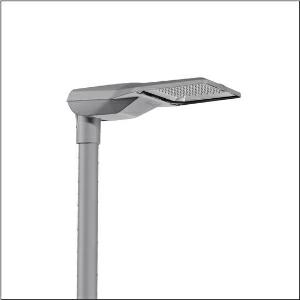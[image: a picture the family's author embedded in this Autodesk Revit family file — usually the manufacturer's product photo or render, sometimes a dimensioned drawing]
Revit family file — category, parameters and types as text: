
# Revit family: streetlight_sl_21_iq_midi___st1_0a_5xe3d31g08nb_2a13
name_source: partatom
category: Lighting Fixtures
units: mm (PartAtom-declared; Revit-internal decimal feet)

## family parameters
Cut with Voids When Loaded = No
Host = Face
Light Source = No
Part Type = Normal
Room Calculation Point = No
Round Connector Dimension = Use Diameter
Shared = No

## types (1)
- --- (1 x LED, 23230 lm, 155.5 W, 3000K)
    Apparent Load = 155 VA
    CIE Flux Codes = 40 73 97 100 100
    Color Rendering = 70
    Color Temperature = 3000K
    Default Elevation = 1800 mm
    Description = Streetlight SL 21 iQ midi, mast luminaire, primary light control with lens, of PMMA, primary optical cover: cover, of toughened safety glass, transparent, light distribution: ST1.0a, light emission: direct distribution, primary light characteristic: asymmetric, installation type: post-top, side-entry, LED, High Power LED, rated luminous flux: 23.230lm, luminous efficacy: 149lm/W, light colour: 730, colour temperature: 3000K, control: Street-Remote, Auto-Match, Temp-Guard, Lumen-Switch, Night-Set, Smart-Wire, Light-Fading, Desk-Remote (wireless, voltage-free reading and setting of iQ features in the workshop via application-optimized NFC function/RFID function), optimised constant luminous flux control (CLO 2.0), presetting dimming linear, mains connection: 230..240V, AC, 50/60Hz, start of lifetime: 156W, end of service life: 162W, reduction: 69W, luminaire housing, of diecast aluminium, powder-coated, Siteco® metallic grey (DB 702S), corrosivity category C5 mid according to DIN EN ISO 12944, please order mast flange separately, inclination adjustable: 0°, 5°, 10°, 15°, sealing non-destructively replaceable, multi-level sealing system, length: 644mm, width: 335mm, height: 110mm, mast flange for spigot size: 42mm (side-entry): 5XC10008XM4, 60/48mm (side-entry/post-top): 5XC10108XM2, 76/60mm (side-entry/post-top): 5XC10108XM1, protection rating (complete): IP66, insulation class (complete): insulation class II (safety insulation), certification: CE, ENEC, ENEC+, VDE, impact resistance: IK09, permissible operating ambient temperature for outdoor applications: -40..+50°C, standard-compliant lighting for roads and squares, packaging unit: 1 piece

Light Distribution: ST1.0a
    Height = 111 mm
    Lamp = 1 x LED
    Lamp Light Flux = 23230 lm
    Lamp Power = 155.5 W
    Lamp count = 1
    Length = 644 mm
    Luminous efficacy = 149 lm/W
    Manufacturer = Siteco
    ModVariant = No
    Model = 5XE3D31G08NB
    Number of Poles = 1
    OnlyDefault = Yes
    Power Factor = 1
    Product Name = Streetlight SL 21 iQ midi | ST1.0a
    Product group = mast luminaire | pylon top
    ProductGroupID = 6100
    Protection Class = Protection class II
    Protection Degree = IP 66
    RLX_Detail_Level = 1
    RLX_Emergency_Light_Flux = 0 lm
    RLX_Emergency_Type = 0
    RLX_Emergency_Type_DB = No
    RlxData = <blob elided: 91081 chars, md5=065021f2>
    Socket = socket
    Standby Power = 0 W
    System Light Flux = 23230 lm
    System Power = 155 W
    Type Comments = factory setting: luminous flux: 100 % | dim-lin: 254 | 823 mA
    Type Image = l_1004298.jpg
    URL = http://relux.com
    VarID = @adj_121435
    Voltage = 0 V
    Weight = 0.00 kg
    Width = 336 mm

## geometry (parser evidence)
native form markers: Blend x4, Sweep x11
no freeform markers — native parametric forms only
